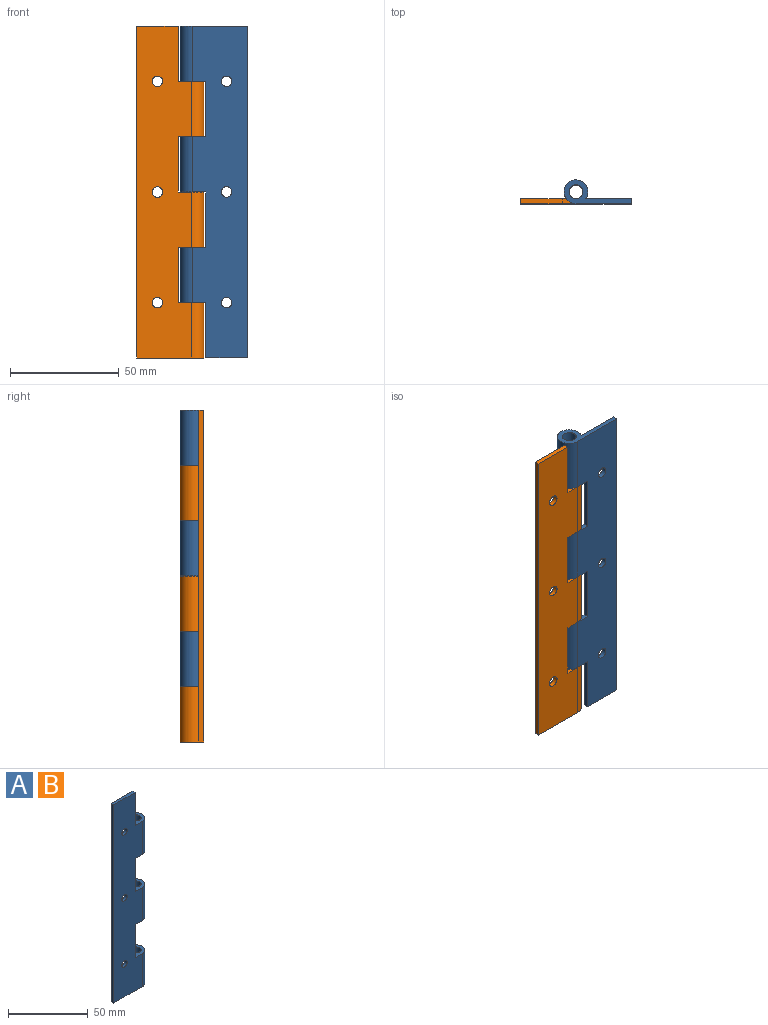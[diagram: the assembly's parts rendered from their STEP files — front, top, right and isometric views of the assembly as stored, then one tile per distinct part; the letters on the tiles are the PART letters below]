
ASSEMBLY  parts=2 mates=1
PART A: 22 faces, bbox 30.9x10.9x152.4 mm
  f0: cylinder r=3.17mm len=25.4mm, axis (0,0,-1), area 506.7mm2, adj f13,f15
  f1: cylinder r=3.17mm len=25.4mm, axis (0,0,-1), area 506.7mm2, adj f17,f19
  f2: cylinder r=3.17mm len=25.4mm, axis (0,0,-1), area 506.7mm2, adj f14,f20
  f3: cylinder r=2.41mm len=4.83mm, axis (0,1,0), area 34.7mm2, adj f9,f10
  f4: cylinder r=2.41mm len=4.83mm, axis (0,1,0), area 34.7mm2, adj f9,f10
  f5: cylinder r=2.41mm len=4.83mm, axis (0,1,0), area 34.7mm2, adj f9,f10
  f6: cylinder r=5.46mm len=25.4mm, axis (0,0,-1), area 739.7mm2, adj f9,f10,f17,f19
  f7: cylinder r=5.46mm len=25.4mm, axis (0,0,-1), area 739.7mm2, adj f9,f10,f13,f15
  f8: cylinder r=5.46mm len=25.4mm, axis (0,0,-1), area 739.7mm2, adj f9,f10,f14,f20
  f9: plane 152.4x25.4mm, normal (0,-1,0), area 3332.2mm2, adj f3,f4,f5,f6,f7,f8,f11,f12
  f10: plane 152.4x20.96mm, normal (0,1,0), area 2993.6mm2, adj f3,f4,f5,f6,f7,f8,f11,f12
  f11: plane 152.4x2.29mm, normal (-1,0,0), area 348.4mm2, adj f9,f10,f12,f13
  f12: plane 19.05x2.29mm, normal (0,0,1), area 43.5mm2, adj f9,f10,f11,f18
  f13: plane 30.86x10.92mm, normal (0,0,-1), area 113mm2, adj f0,f7,f9,f10,f11
  f14: plane 11.81x10.92mm, normal (0,0,-1), area 69.4mm2, adj f2,f8,f9,f10,f16
  f15: plane 11.81x10.92mm, normal (0,0,1), area 69.4mm2, adj f0,f7,f9,f10,f16
  f16: plane 25.4x2.29mm, normal (1,0,0), area 58.1mm2, adj f9,f10,f14,f15
  f17: plane 11.81x10.92mm, normal (0,0,1), area 69.4mm2, adj f1,f6,f9,f10,f18
  f18: plane 25.4x2.29mm, normal (1,0,0), area 58.1mm2, adj f9,f10,f12,f17
  f19: plane 11.81x10.92mm, normal (0,0,-1), area 69.4mm2, adj f1,f6,f9,f10,f21
  f20: plane 11.81x10.92mm, normal (0,0,1), area 69.4mm2, adj f2,f8,f9,f10,f21
  f21: plane 25.4x2.29mm, normal (1,0,0), area 58.1mm2, adj f9,f10,f19,f20
PART B: same geometry as A
PLACE A rot(axis=(0,1,0),180deg) t=(70.66,116.02,264.13)mm
PLACE B t=(19.86,116.02,111.73)mm fixed
MATE revolute B.f0 <-> A.f0  axis (0,0,1) through (45.26,121.48,238.73)mm
